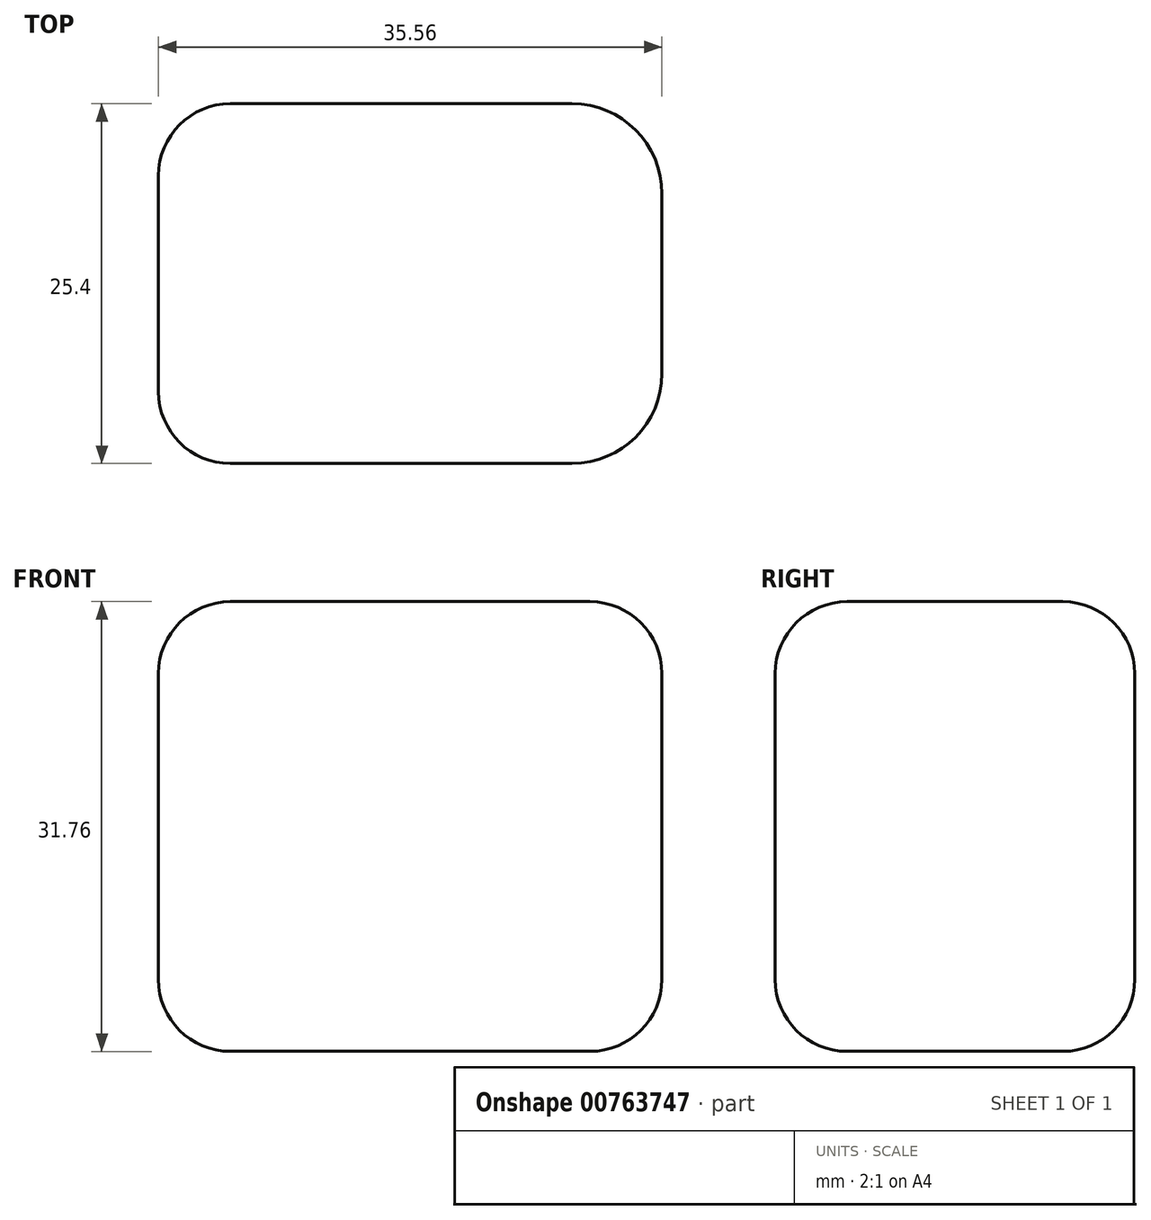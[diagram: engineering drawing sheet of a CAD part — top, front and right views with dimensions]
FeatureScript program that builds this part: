
annotation { "Feature Type Name" : "Feature", "Feature Type Description" : "" }
export const myFeature = defineFeature(function(context is Context, id is Id, definition is map)
    precondition{}
    {
        {
            var Q0;
            Q0=qCreatedBy(makeId("Front.planeOp"),FACE);
            var sketch = newSketch(context, id + "F0", { "sketchPlane" : qUnion([Q0])});
            skLineSegment(sketch, "E0.bottom", {"start": v(17.78, -15.88) * mm, "end": v(-17.78, -15.88) * mm});
            skLineSegment(sketch, "E0.top", {"start": v(17.78, 15.88) * mm, "end": v(-17.78, 15.88) * mm});
            skLineSegment(sketch, "E0.left", {"start": v(17.78, -15.88) * mm, "end": v(17.78, 15.88) * mm});
            skLineSegment(sketch, "E0.right", {"start": v(-17.78, -15.88) * mm, "end": v(-17.78, 15.87) * mm});
            skPoint(sketch, "E0.middle", {"position": v(0, 0) * mm});
            skSolve(sketch);
        }
        {
            var Q0;
            Q0 = qSketchRegion(id + "F0", true);
            extrude(context, id + "F1", {"entities" : qUnion([Q0]), "endBound" : BoundingType.SYMMETRIC, "depth" : 25.4 * mm, "offsetDistance" : 25.4 * mm});
        }
        {
            var Q0;
            Q0=makeQuery(id+"F1.opExtrude","CAP_EDGE",EDGE,{"disambiguationData":[OSD([sQuery(id+"F0.wireOp",EDGE,"E0.top")])],"isStart":false});
            var Q1;
            Q1=makeQuery(id+"F1.opExtrude","CAP_EDGE",EDGE,{"disambiguationData":[OSD([sQuery(id+"F0.wireOp",EDGE,"E0.top")])],"isStart":true});
            var Q2;
            Q2=makeQuery(id+"F1.opExtrude","SWEPT_EDGE",EDGE,{"disambiguationData":[OSD([sQuery(id+"F0.wireOp",EDGE,"E0.top"),sQuery(id+"F0.wireOp",EDGE,"E0.left")])]});
            fillet(context, id + "F2", {"entities" : qUnion([Q0, Q1, Q2]), "radius" : 5.08 * mm, "tangentPropagation" : true, "allowEdgeOverflow" : false});
        }
        {
            var Q0;
            Q0=makeQuery(id+"F1.opExtrude","CAP_EDGE",EDGE,{"disambiguationData":[OSD([sQuery(id+"F0.wireOp",EDGE,"E0.left")])],"isStart":false});
            var Q1;
            Q1=makeQuery(id+"F1.opExtrude","CAP_EDGE",EDGE,{"disambiguationData":[OSD([sQuery(id+"F0.wireOp",EDGE,"E0.left")])],"isStart":true});
            fillet(context, id + "F3", {"entities" : qUnion([Q0, Q1]), "radius" : 6.35 * mm, "tangentPropagation" : true, "allowEdgeOverflow" : false});
        }
        {
            var Q0;
            Q0=makeQuery(id+"F1.opExtrude","SWEPT_EDGE",EDGE,{"disambiguationData":[OSD([sQuery(id+"F0.wireOp",EDGE,"E0.bottom"),sQuery(id+"F0.wireOp",EDGE,"E0.right")])]});
            fillet(context, id + "F4", {"entities" : qUnion([Q0]), "radius" : 5.08 * mm, "tangentPropagation" : true, "allowEdgeOverflow" : false});
        }
        {
            var Q0;
            {var subQ0=sQuery(id+"F0.wireOp",EDGE,"E0.right");var subQ1=sQuery(id+"F0.wireOp",EDGE,"E0.bottom");Q0=makeQuery(id+"F4.opFillet","BLEND_EDGE",EDGE,{"blendedFrom":[makeQuery(id+"F1.opExtrude","SWEPT_EDGE",EDGE,{"disambiguationData":[OSD([subQ1,subQ0])]}),makeQuery(id+"F1.opExtrude","CAP_FACE",FACE,{"disambiguationData":[OSD([subQ1,sQuery(id+"F0.wireOp",EDGE,"E0.top"),sQuery(id+"F0.wireOp",EDGE,"E0.left"),subQ0])],"isStart":false})],"blendedInto":[makeQuery(id+"F1.opExtrude","CAP_FACE",FACE,{"disambiguationData":[OSD([subQ1,sQuery(id+"F0.wireOp",EDGE,"E0.top"),sQuery(id+"F0.wireOp",EDGE,"E0.left"),subQ0])],"isStart":false})]});}
            var Q1;
            {var subQ0=sQuery(id+"F0.wireOp",EDGE,"E0.right");var subQ1=sQuery(id+"F0.wireOp",EDGE,"E0.bottom");Q1=makeQuery(id+"F4.opFillet","BLEND_EDGE",EDGE,{"blendedFrom":[makeQuery(id+"F1.opExtrude","SWEPT_EDGE",EDGE,{"disambiguationData":[OSD([subQ1,subQ0])]}),makeQuery(id+"F1.opExtrude","CAP_FACE",FACE,{"disambiguationData":[OSD([subQ1,sQuery(id+"F0.wireOp",EDGE,"E0.top"),sQuery(id+"F0.wireOp",EDGE,"E0.left"),subQ0])],"isStart":true})],"blendedInto":[makeQuery(id+"F1.opExtrude","CAP_FACE",FACE,{"disambiguationData":[OSD([subQ1,sQuery(id+"F0.wireOp",EDGE,"E0.top"),sQuery(id+"F0.wireOp",EDGE,"E0.left"),subQ0])],"isStart":true})]});}
            fillet(context, id + "F5", {"entities" : qUnion([Q0, Q1]), "radius" : 5.08 * mm, "tangentPropagation" : true, "allowEdgeOverflow" : false});
        }
    });
